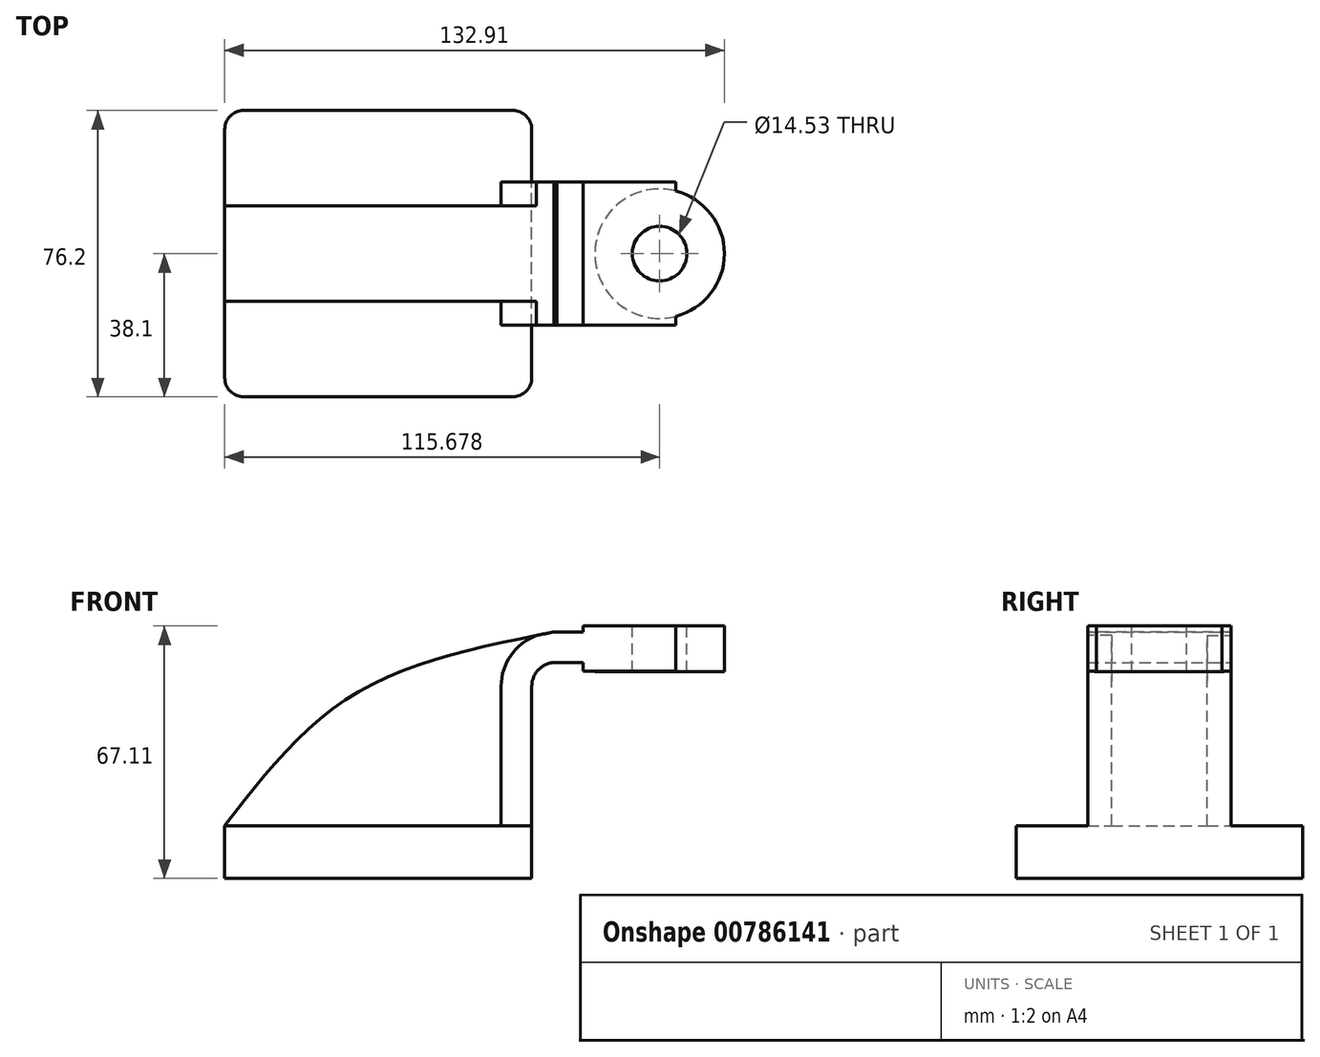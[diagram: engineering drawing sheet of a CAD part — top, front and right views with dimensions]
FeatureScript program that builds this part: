
annotation { "Feature Type Name" : "Feature", "Feature Type Description" : "" }
export const myFeature = defineFeature(function(context is Context, id is Id, definition is map)
    precondition{}
    {
        {
            var Q0;
            Q0=qCreatedBy(makeId("Front.planeOp"),FACE);
            var sketch = newSketch(context, id + "F0", { "sketchPlane" : qUnion([Q0])});
            skLineSegment(sketch, "E0.bottom", {"start": v(40.84, -7) * mm, "end": v(-40.84, -7) * mm});
            skLineSegment(sketch, "E0.top", {"start": v(40.84, 7) * mm, "end": v(-40.84, 7) * mm});
            skLineSegment(sketch, "E0.left", {"start": v(40.84, -7) * mm, "end": v(40.84, 7) * mm});
            skLineSegment(sketch, "E0.right", {"start": v(-40.84, -7) * mm, "end": v(-40.84, 7) * mm});
            skPoint(sketch, "E0.middle", {"position": v(0, 0) * mm});
            skLineSegment(sketch, "E1.bottom", {"start": v(79.1, 48.12) * mm, "end": v(54.54, 48.12) * mm});
            skLineSegment(sketch, "E1.top", {"start": v(79.1, 60.11) * mm, "end": v(54.54, 60.11) * mm});
            skLineSegment(sketch, "E1.left", {"start": v(79.1, 48.12) * mm, "end": v(79.1, 60.11) * mm});
            skLineSegment(sketch, "E1.right", {"start": v(54.54, 48.12) * mm, "end": v(54.54, 60.11) * mm});
            skPoint(sketch, "E1.middle", {"position": v(66.82, 54.12) * mm});
            skLineSegment(sketch, "E2", {"start": v(40.84, 7) * mm, "end": v(40.84, 44.12) * mm});
            skLineSegment(sketch, "E3", {"start": v(66.82, 50.4) * mm, "end": v(47.4, 50.4) * mm});
            skArc(sketch, "E4", {"start": v(47.4, 50.4) * mm, "mid": v(42.78, 48.67) * mm, "end": v(40.84, 44.12) * mm});
            skLineSegment(sketch, "E5.0", {"start": v(32.7, 7) * mm, "end": v(32.7, 44.12) * mm});
            skArc(sketch, "E5.1", {"start": v(47.55, 58.53) * mm, "mid": v(37.08, 54.46) * mm, "end": v(32.7, 44.12) * mm});
            skLineSegment(sketch, "E5.2", {"start": v(66.82, 58.53) * mm, "end": v(47.55, 58.53) * mm});
            skFitSpline(sketch, "E6", {"points": [v(-40.84, 7) * mm, v(-6.57, 41.84) * mm, v(46.7, 58.53) * mm], "startDerivative": vector(63.1, 81.69) * mm, "endDerivative": vector(111.43, 22.04) * mm});
            skSolve(sketch);
        }
        {
            var Q0;
            Q0=makeQuery(id+"F0.imprint","IMPRINT",FACE,{"disambiguationData":[TD([[makeQuery(id+"F0.imprint","IMPRINT",EDGE,{"derivedFrom":sQuery(id+"F0.wireOp",EDGE,"E0.bottom")}),-1.0]])]});
            extrude(context, id + "F1", {"entities" : qUnion([Q0]), "endBound" : BoundingType.SYMMETRIC, "depth" : 76.2 * mm, "offsetDistance" : 25.4 * mm});
        }
        {
            var Q0;
            {var subQ4=sQuery(id+"F0.wireOp",EDGE,"E2");Q0=makeQuery(id+"F0.imprint","IMPRINT",FACE,{"disambiguationData":[TD([[makeQuery(id+"F0.imprint","IMPRINT",EDGE,{"derivedFrom":subQ4}),1.0]])]});}
            var Q1;
            {var subQ1=sQuery(id+"F0.wireOp",EDGE,"E1.bottom");Q1=makeQuery(id+"F0.imprint","IMPRINT",FACE,{"disambiguationData":[TD([[makeQuery(id+"F0.imprint","IMPRINT",EDGE,{"derivedFrom":subQ1}),-1.0]])]});}
            extrude(context, id + "F2", {"entities" : qUnion([Q0, Q1]), "operationType" : NewBodyOperationType.ADD, "endBound" : BoundingType.SYMMETRIC, "depth" : 38.1 * mm, "offsetDistance" : 25.4 * mm});
        }
        {
            var Q0;
            {var subQ3=sQuery(id+"F0.wireOp",EDGE,"E5.0");Q0=makeQuery(id+"F0.imprint","IMPRINT",FACE,{"disambiguationData":[TD([[makeQuery(id+"F0.imprint","IMPRINT",EDGE,{"derivedFrom":subQ3}),1.0]])]});}
            extrude(context, id + "F3", {"entities" : qUnion([Q0]), "operationType" : NewBodyOperationType.ADD, "endBound" : BoundingType.SYMMETRIC, "depth" : 25.4 * mm, "offsetDistance" : 25.4 * mm});
        }
        {
            var Q0;
            Q0=makeQuery(id+"F2.opExtrude","SWEPT_FACE",FACE,{"disambiguationData":[OSD([sQuery(id+"F0.wireOp",EDGE,"E1.top")])]});
            var sketch = newSketch(context, id + "F4", { "sketchPlane" : qUnion([Q0])});
            skCircle(sketch, "E7", {"center": v(74.84, 0) * mm, "radius": 17.23 * mm});
            skSolve(sketch);
        }
        {
            var Q0;
            {var subQ0=sQuery(id+"F4.wireOp",EDGE,"E7");var subQ1=makeQuery(id+"F2.opExtrude","SWEPT_EDGE",EDGE,{"disambiguationData":[OSD([sQuery(id+"F0.wireOp",EDGE,"E1.top"),sQuery(id+"F0.wireOp",EDGE,"E1.left")])]});var subQ2=makeQuery(id+"F4.imprint","INTERSECT",VERTEX,{"disambiguationData":[OD(0.0)],"derivedFrom":[subQ1,subQ0]});Q0=makeQuery(id+"F4.imprint","IMPRINT",FACE,{"disambiguationData":[TD([[makeQuery(id+"F4.imprint","IMPRINT",EDGE,{"disambiguationData":[TD([[subQ2,1.0]])],"derivedFrom":subQ0}),1.0]])]});}
            var Q1;
            {var subQ0=sQuery(id+"F4.wireOp",EDGE,"E7");var subQ1=makeQuery(id+"F2.opExtrude","SWEPT_EDGE",EDGE,{"disambiguationData":[OSD([sQuery(id+"F0.wireOp",EDGE,"E1.top"),sQuery(id+"F0.wireOp",EDGE,"E1.left")])]});var subQ2=makeQuery(id+"F4.imprint","INTERSECT",VERTEX,{"disambiguationData":[OD(0.0)],"derivedFrom":[subQ1,subQ0]});Q1=makeQuery(id+"F4.imprint","IMPRINT",FACE,{"disambiguationData":[TD([[makeQuery(id+"F4.imprint","IMPRINT",EDGE,{"disambiguationData":[TD([[subQ2,-1.0]])],"derivedFrom":subQ0}),1.0]])]});}
            extrude(context, id + "F5", {"entities" : qUnion([Q0, Q1]), "operationType" : NewBodyOperationType.ADD, "oppositeDirection" : true, "depth" : 12.2 * mm, "offsetDistance" : 25.4 * mm});
        }
        {
            var Q0;
            Q0=makeQuery(id+"F1.opExtrude","CAP_EDGE",EDGE,{"disambiguationData":[OSD([sQuery(id+"F0.wireOp",EDGE,"E0.right")])],"isStart":false});
            var Q1;
            Q1=makeQuery(id+"F1.opExtrude","CAP_EDGE",EDGE,{"disambiguationData":[OSD([sQuery(id+"F0.wireOp",EDGE,"E0.left")])],"isStart":false});
            var Q2;
            Q2=makeQuery(id+"F1.opExtrude","CAP_EDGE",EDGE,{"disambiguationData":[OSD([sQuery(id+"F0.wireOp",EDGE,"E0.left")])],"isStart":true});
            var Q3;
            Q3=makeQuery(id+"F1.opExtrude","CAP_EDGE",EDGE,{"disambiguationData":[OSD([sQuery(id+"F0.wireOp",EDGE,"E0.right")])],"isStart":true});
            fillet(context, id + "F6", {"entities" : qUnion([Q0, Q1, Q2, Q3]), "radius" : 5.08 * mm, "tangentPropagation" : true, "allowEdgeOverflow" : false});
        }
        {
            var Q0;
            Q0=makeQuery(id+"F5.boolean.opBoolean","MERGE",FACE,{"derivedFrom":[makeQuery(id+"F2.opExtrude","SWEPT_FACE",FACE,{"disambiguationData":[OSD([sQuery(id+"F0.wireOp",EDGE,"E1.top")])]}),makeQuery(id+"F5.opExtrude","CAP_FACE",FACE,{"disambiguationData":[OSD([sQuery(id+"F4.wireOp",EDGE,"E7")])],"isStart":true})]});
            var sketch = newSketch(context, id + "F7", { "sketchPlane" : qUnion([Q0])});
            skCircle(sketch, "E8", {"center": v(74.84, 0) * mm, "radius": 7.27 * mm});
            skSolve(sketch);
        }
        {
            var Q0;
            Q0=makeQuery(id+"F7.imprint","IMPRINT",FACE,{"disambiguationData":[TD([[makeQuery(id+"F7.imprint","IMPRINT",EDGE,{"derivedFrom":sQuery(id+"F7.wireOp",EDGE,"E8")}),1.0]])]});
            extrude(context, id + "F8", {"entities" : qUnion([Q0]), "operationType" : NewBodyOperationType.REMOVE, "endBound" : BoundingType.THROUGH_ALL, "oppositeDirection" : true, "depth" : 25.4 * mm, "offsetDistance" : 25.4 * mm});
        }
    });
